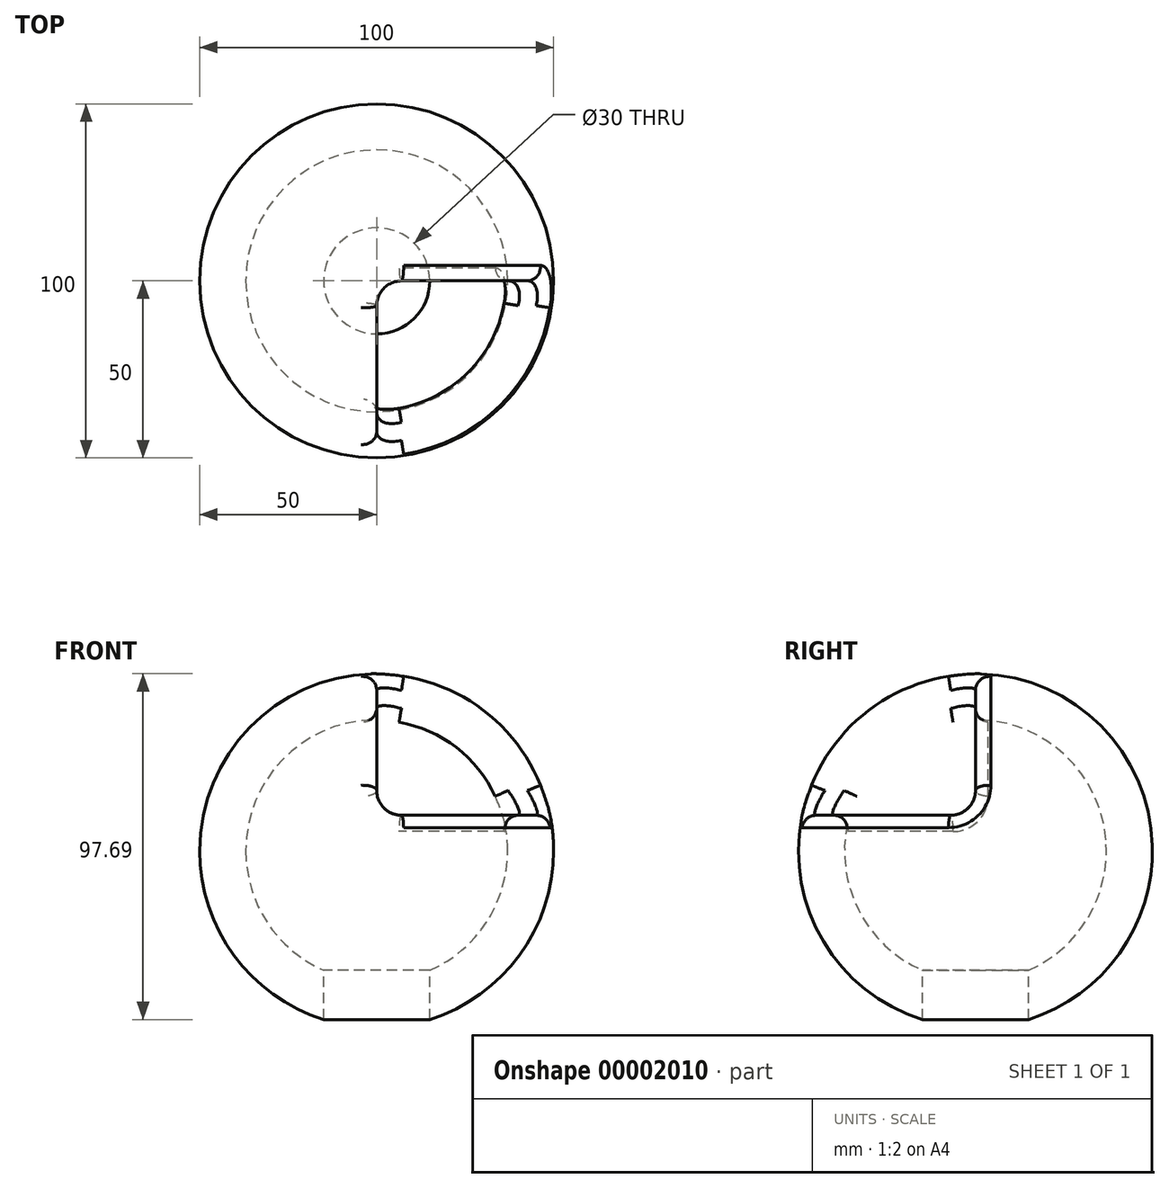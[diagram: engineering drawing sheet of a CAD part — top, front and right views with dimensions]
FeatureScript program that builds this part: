
annotation { "Feature Type Name" : "Feature", "Feature Type Description" : "" }
export const myFeature = defineFeature(function(context is Context, id is Id, definition is map)
    precondition{}
    {
        {
            var Q0;
            Q0=qCreatedBy(makeId("Top.planeOp"),FACE);
            var sketch = newSketch(context, id + "F0", { "sketchPlane" : qUnion([Q0])});
            skLineSegment(sketch, "E0", {"start": v(0, 0) * mm, "end": v(152.88, 0) * mm, "construction": true});
            skArc(sketch, "E1", {"start": v(50, 0) * mm, "mid": v(0, 50) * mm, "end": v(-50, 0) * mm});
            skArc(sketch, "E2", {"start": v(37, 0) * mm, "mid": v(0, 37) * mm, "end": v(-37, 0) * mm});
            skLineSegment(sketch, "E3", {"start": v(-50, 0) * mm, "end": v(-37, 0) * mm});
            skLineSegment(sketch, "E4", {"start": v(37, 0) * mm, "end": v(50, 0) * mm});
            skSolve(sketch);
        }
        {
            var Q0;
            Q0=makeQuery(id+"F0.imprint","IMPRINT",FACE,{"disambiguationData":[TD([[makeQuery(id+"F0.imprint","IMPRINT",EDGE,{"derivedFrom":sQuery(id+"F0.wireOp",EDGE,"E1")}),1.0]])]});
            var Q1;
            Q1=sQuery(id+"F0.wireOp",EDGE,"E0");
            revolve(context, id + "F1", {"entities" : qUnion([Q0]), "axis" : qUnion([Q1]), "revolveType" : RevolveType.FULL});
        }
        {
            var Q0;
            Q0=qCreatedBy(makeId("Top.planeOp"),FACE);
            cPlane(context, id + "F2", {"entities" : qUnion([Q0]), "cplaneType" : CPlaneType.OFFSET, "offset" : 10 * mm, "width" : 150 * mm, "height" : 150 * mm});
        }
        {
            var Q0;
            Q0=qCreatedBy(id+"F2.planeOp",FACE);
            var sketch = newSketch(context, id + "F3", { "sketchPlane" : qUnion([Q0])});
            skLineSegment(sketch, "E5.bottom", {"start": v(0, 0) * mm, "end": v(60.45, 0) * mm});
            skLineSegment(sketch, "E5.top", {"start": v(0, -60.59) * mm, "end": v(60.45, -60.59) * mm});
            skLineSegment(sketch, "E5.left", {"start": v(0, 0) * mm, "end": v(0, -60.59) * mm});
            skLineSegment(sketch, "E5.right", {"start": v(60.45, 0) * mm, "end": v(60.45, -60.59) * mm});
            skSolve(sketch);
        }
        {
            var Q0;
            Q0 = qSketchRegion(id + "F3", true);
            extrude(context, id + "F4", {"entities" : qUnion([Q0]), "operationType" : NewBodyOperationType.REMOVE, "depth" : 50 * mm});
        }
        {
            var Q0;
            Q0=makeQuery(id+"F4.boolean.opBoolean","COPY",EDGE,{"derivedFrom":makeQuery(id+"F4.opExtrude","SWEPT_EDGE",EDGE,{"disambiguationData":[OSD([sQuery(id+"F3.wireOp",EDGE,"E5.bottom"),sQuery(id+"F3.wireOp",EDGE,"E5.left")])]})});
            var Q1;
            Q1=makeQuery(id+"F4.boolean.opBoolean","COPY",EDGE,{"derivedFrom":makeQuery(id+"F4.opExtrude","CAP_EDGE",EDGE,{"disambiguationData":[OSD([sQuery(id+"F3.wireOp",EDGE,"E5.bottom")])],"isStart":true})});
            var Q2;
            Q2=makeQuery(id+"F4.boolean.opBoolean","COPY",EDGE,{"derivedFrom":makeQuery(id+"F4.opExtrude","CAP_EDGE",EDGE,{"disambiguationData":[OSD([sQuery(id+"F3.wireOp",EDGE,"E5.left")])],"isStart":true})});
            fillet(context, id + "F5", {"entities" : qUnion([Q0, Q1, Q2]), "radius" : 7 * mm, "allowEdgeOverflow" : false});
        }
        {
            var Q0;
            Q0=makeQuery(id+"F4.boolean.opBoolean","INTERSECT",EDGE,{"derivedFrom":[makeQuery(id+"F1.opRevolve","SWEPT_FACE",FACE,{"disambiguationData":[OSD([sQuery(id+"F0.wireOp",EDGE,"E1")])]}),makeQuery(id+"F4.opExtrude","SWEPT_FACE",FACE,{"disambiguationData":[OSD([sQuery(id+"F3.wireOp",EDGE,"E5.left")])]})]});
            var Q1;
            Q1=makeQuery(id+"F4.boolean.opBoolean","INTERSECT",EDGE,{"derivedFrom":[makeQuery(id+"F1.opRevolve","SWEPT_FACE",FACE,{"disambiguationData":[OSD([sQuery(id+"F0.wireOp",EDGE,"E2")])]}),makeQuery(id+"F4.opExtrude","SWEPT_FACE",FACE,{"disambiguationData":[OSD([sQuery(id+"F3.wireOp",EDGE,"E5.left")])]})]});
            fillet(context, id + "F6", {"entities" : qUnion([Q0, Q1]), "radius" : 4 * mm, "tangentPropagation" : true, "allowEdgeOverflow" : false});
        }
        {
            var Q0;
            Q0=qCreatedBy(makeId("Top.planeOp"),FACE);
            var sketch = newSketch(context, id + "F7", { "sketchPlane" : qUnion([Q0])});
            skCircle(sketch, "E6", {"center": v(0, 0) * mm, "radius": 15 * mm});
            skSolve(sketch);
        }
        {
            var Q0;
            Q0 = qSketchRegion(id + "F7", true);
            extrude(context, id + "F8", {"entities" : qUnion([Q0]), "operationType" : NewBodyOperationType.REMOVE, "oppositeDirection" : true, "depth" : 60 * mm});
        }
    });
